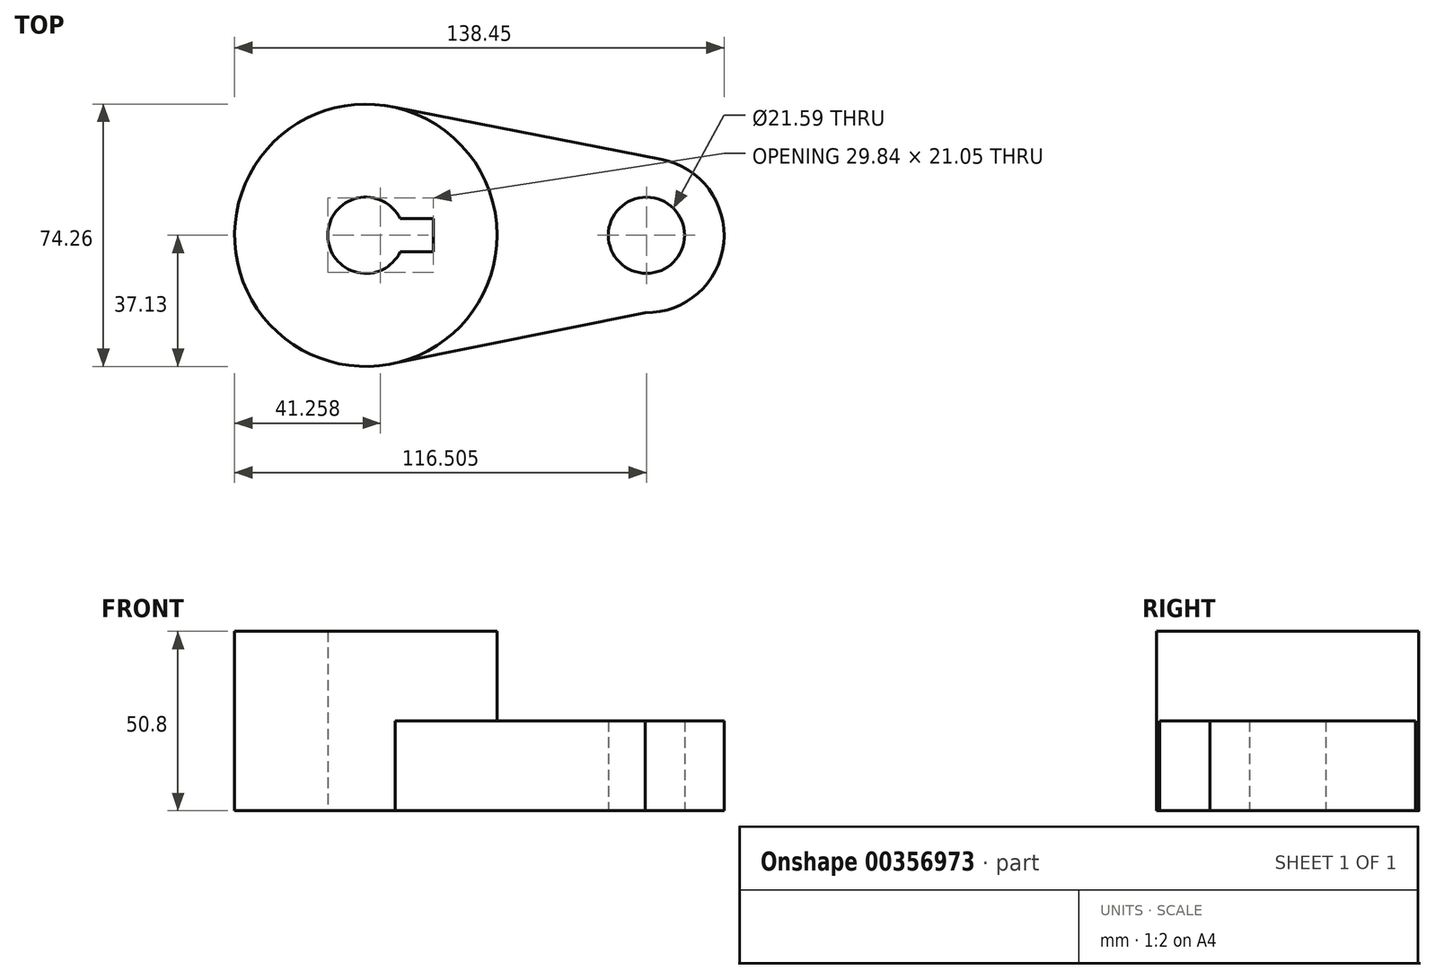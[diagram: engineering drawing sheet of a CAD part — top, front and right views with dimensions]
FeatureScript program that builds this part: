
annotation { "Feature Type Name" : "Feature", "Feature Type Description" : "" }
export const myFeature = defineFeature(function(context is Context, id is Id, definition is map)
    precondition{}
    {
        {
            var Q0;
            Q0=qCreatedBy(makeId("Top.planeOp"),FACE);
            var sketch = newSketch(context, id + "F0", { "sketchPlane" : qUnion([Q0])});
            skCircle(sketch, "E0", {"center": v(0, 0) * mm, "radius": 1.43 * mm});
            skCircle(sketch, "E1", {"center": v(0, 0) * mm, "radius": 37.13 * mm});
            skCircle(sketch, "E2", {"center": v(79.38, 0) * mm, "radius": 21.94 * mm});
            skLineSegment(sketch, "E3", {"start": v(8.27, 36.2) * mm, "end": v(83.57, 21.54) * mm});
            skLineSegment(sketch, "E4", {"start": v(8.27, -36.2) * mm, "end": v(79.03, -21.94) * mm});
            skCircle(sketch, "E5", {"center": v(0, 0) * mm, "radius": 10.8 * mm});
            skCircle(sketch, "E6", {"center": v(79.38, 0) * mm, "radius": 10.8 * mm});
            skLineSegment(sketch, "E7.bottom", {"start": v(19.05, 4.7) * mm, "end": v(-19.05, 4.7) * mm});
            skLineSegment(sketch, "E7.top", {"start": v(19.05, -4.7) * mm, "end": v(-19.05, -4.7) * mm});
            skLineSegment(sketch, "E7.left", {"start": v(19.05, 4.7) * mm, "end": v(19.05, -4.7) * mm});
            skLineSegment(sketch, "E7.right", {"start": v(-19.05, 4.7) * mm, "end": v(-19.05, -4.7) * mm});
            skSolve(sketch);
        }
        {
            var Q0;
            {var subQ5=sQuery(id+"F0.wireOp",EDGE,"E7.right");Q0=makeQuery(id+"F0.imprint","IMPRINT",FACE,{"disambiguationData":[TD([[makeQuery(id+"F0.imprint","IMPRINT",EDGE,{"derivedFrom":subQ5}),1.0]])]});}
            var Q1;
            {var subQ7=sQuery(id+"F0.wireOp",EDGE,"E7.left");Q1=makeQuery(id+"F0.imprint","IMPRINT",FACE,{"disambiguationData":[TD([[makeQuery(id+"F0.imprint","IMPRINT",EDGE,{"derivedFrom":subQ7}),1.0]])]});}
            var Q2;
            Q2=makeQuery(id+"F0.imprint","IMPRINT",FACE,{"disambiguationData":[TD([[makeQuery(id+"F0.imprint","IMPRINT",EDGE,{"derivedFrom":sQuery(id+"F0.wireOp",EDGE,"E6")}),-1.0]])]});
            var Q3;
            {var subQ0=sQuery(id+"F0.wireOp",EDGE,"E3");Q3=makeQuery(id+"F0.imprint","IMPRINT",FACE,{"disambiguationData":[TD([[makeQuery(id+"F0.imprint","IMPRINT",EDGE,{"derivedFrom":subQ0}),-1.0]])]});}
            extrude(context, id + "F1", {"entities" : qUnion([Q0, Q1, Q2, Q3]), "depth" : 25.4 * mm});
        }
        {
            var Q0;
            {var subQ7=sQuery(id+"F0.wireOp",EDGE,"E7.left");Q0=makeQuery(id+"F0.imprint","IMPRINT",FACE,{"disambiguationData":[TD([[makeQuery(id+"F0.imprint","IMPRINT",EDGE,{"derivedFrom":subQ7}),1.0]])]});}
            var Q1;
            {var subQ5=sQuery(id+"F0.wireOp",EDGE,"E7.right");Q1=makeQuery(id+"F0.imprint","IMPRINT",FACE,{"disambiguationData":[TD([[makeQuery(id+"F0.imprint","IMPRINT",EDGE,{"derivedFrom":subQ5}),1.0]])]});}
            extrude(context, id + "F2", {"entities" : qUnion([Q0, Q1]), "operationType" : NewBodyOperationType.ADD, "depth" : 50.8 * mm});
        }
    });
